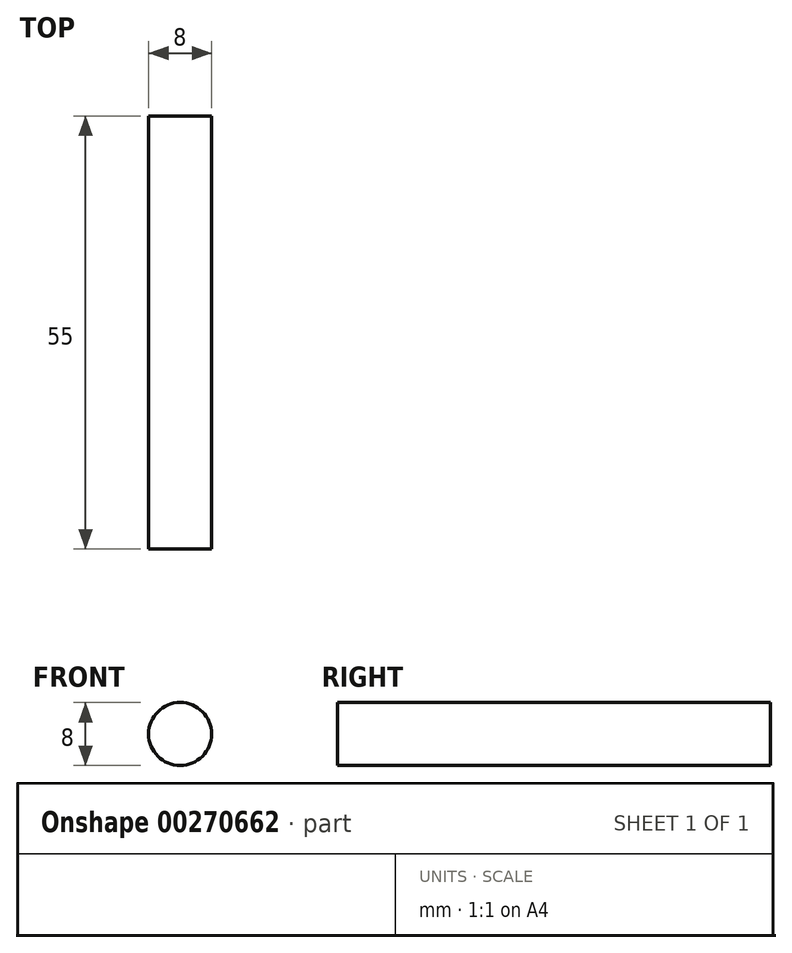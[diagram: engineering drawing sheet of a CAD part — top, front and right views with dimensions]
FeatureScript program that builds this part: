
annotation { "Feature Type Name" : "Feature", "Feature Type Description" : "" }
export const myFeature = defineFeature(function(context is Context, id is Id, definition is map)
    precondition{}
    {
        {
            var Q0;
            Q0=qCreatedBy(makeId("Front.planeOp"),FACE);
            var sketch = newSketch(context, id + "F0", { "sketchPlane" : qUnion([Q0])});
            skCircle(sketch, "E0", {"center": v(0, 0) * mm, "radius": 4 * mm});
            skSolve(sketch);
        }
        {
            var Q0;
            Q0=makeQuery(id+"F0.imprint","IMPRINT",FACE,{"disambiguationData":[TD([[makeQuery(id+"F0.imprint","IMPRINT",EDGE,{"derivedFrom":sQuery(id+"F0.wireOp",EDGE,"E0")}),1.0]])]});
            extrude(context, id + "F1", {"entities" : qUnion([Q0]), "depth" : 55 * mm});
        }
    });
